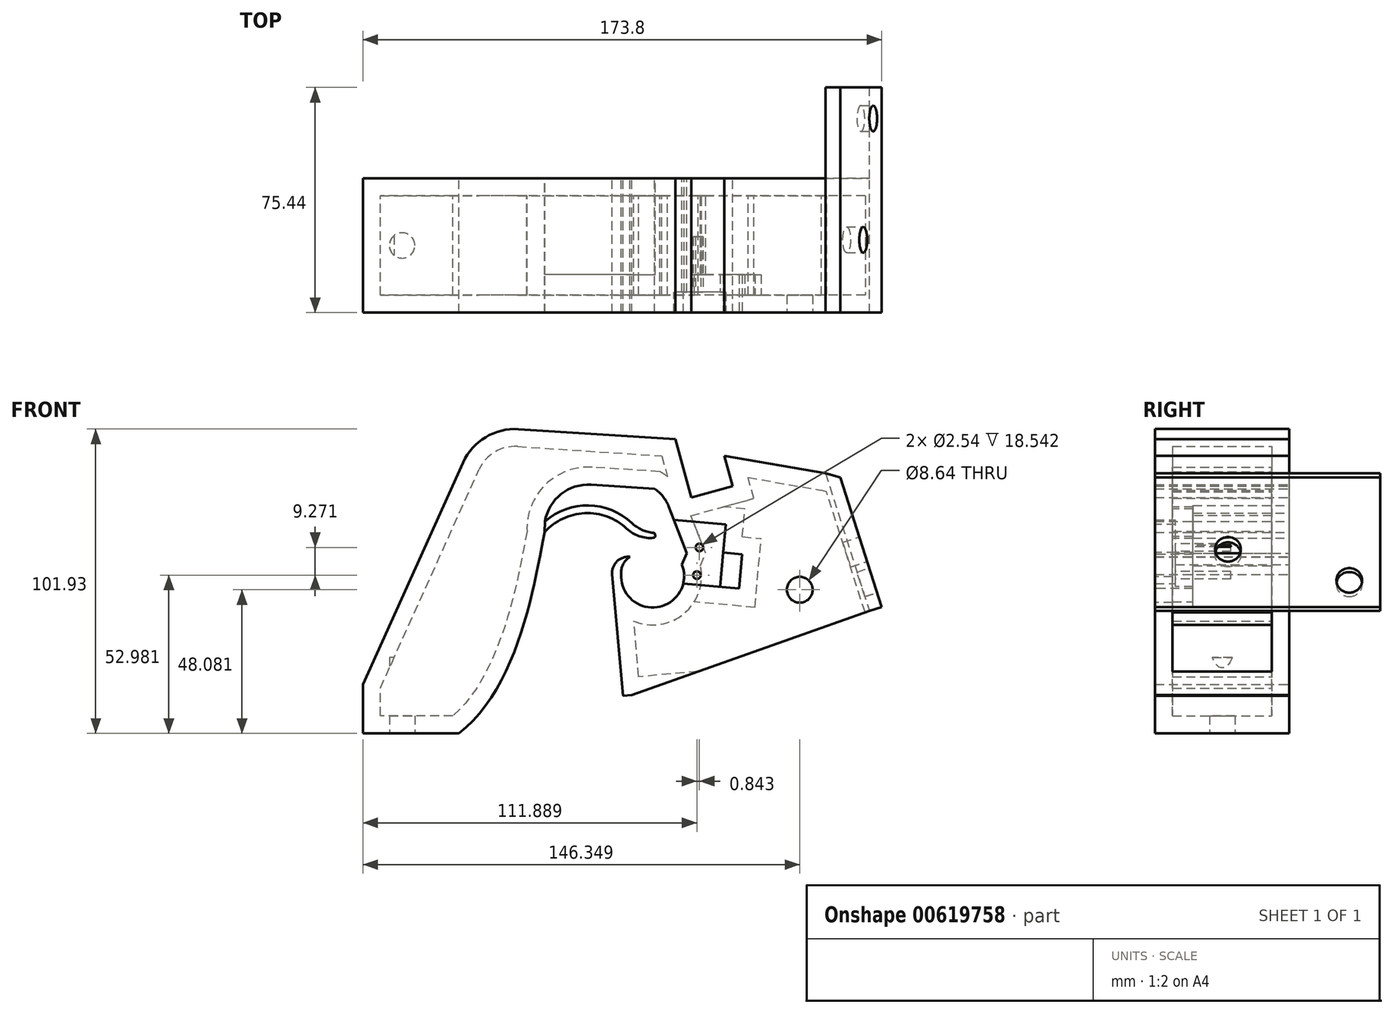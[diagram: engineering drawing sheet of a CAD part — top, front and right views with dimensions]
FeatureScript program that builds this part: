
annotation { "Feature Type Name" : "Feature", "Feature Type Description" : "" }
export const myFeature = defineFeature(function(context is Context, id is Id, definition is map)
    precondition{}
    {
        {
            var Q0;
            Q0=qCreatedBy(makeId("Front.planeOp"),FACE);
            var sketch = newSketch(context, id + "F0", { "sketchPlane" : qUnion([Q0])});
            skLineSegment(sketch, "E0", {"start": v(-44.32, -75.48) * mm, "end": v(-76.5, -75.48) * mm});
            skLineSegment(sketch, "E1", {"start": v(-76.5, -75.48) * mm, "end": v(-76.5, -59.1) * mm});
            skLineSegment(sketch, "E2", {"start": v(-76.5, -59.1) * mm, "end": v(-42.93, 15.25) * mm});
            skLineSegment(sketch, "E3", {"start": v(-24.33, 26.41) * mm, "end": v(28.17, 23.01) * mm});
            skLineSegment(sketch, "E4", {"start": v(28.17, 23.01) * mm, "end": v(33.5, 3.51) * mm});
            skLineSegment(sketch, "E5", {"start": v(33.5, 3.51) * mm, "end": v(47.3, 7.28) * mm});
            skLineSegment(sketch, "E6", {"start": v(47.3, 7.28) * mm, "end": v(44.5, 17.52) * mm});
            skLineSegment(sketch, "E7", {"start": v(44.5, 17.52) * mm, "end": v(78.44, 11.64) * mm});
            skLineSegment(sketch, "E8", {"start": v(93.17, -34.52) * mm, "end": v(13.6, -62.6) * mm});
            skLineSegment(sketch, "E9", {"start": v(10.3, -25.22) * mm, "end": v(10.04, -22.24) * mm});
            skPoint(sketch, "E10", {"position": v(20.57, -22.81) * mm});
            skArc(sketch, "E11", {"start": v(10.04, -22.24) * mm, "mid": v(22.25, -33.23) * mm, "end": v(30.39, -18.96) * mm});
            skArc(sketch, "E12", {"start": v(10.04, -22.24) * mm, "mid": v(10.66, -18.9) * mm, "end": v(12.94, -16.38) * mm});
            skLineSegment(sketch, "E13", {"start": v(30.39, -18.96) * mm, "end": v(32.03, -15.11) * mm});
            skLineSegment(sketch, "E14", {"start": v(32.03, -15.11) * mm, "end": v(25.9, 0.62) * mm});
            skArc(sketch, "E15", {"start": v(25.9, 0.62) * mm, "mid": v(24, 3.89) * mm, "end": v(21.2, 6.44) * mm});
            skLineSegment(sketch, "E16", {"start": v(21.2, 6.44) * mm, "end": v(0, 7.81) * mm});
            skArc(sketch, "E17", {"start": v(0, 7.81) * mm, "mid": v(-10.11, 4.65) * mm, "end": v(-15.5, -4.47) * mm});
            skFitSpline(sketch, "E18", {"points": [v(-15.65, -8.2) * mm, v(-44.32, -75.48) * mm], "startDerivative": vector(-10.53, -56.17) * mm, "endDerivative": vector(-57.92, -43.88) * mm});
            skLineSegment(sketch, "E19", {"start": v(13.6, -62.6) * mm, "end": v(10.6, -62.87) * mm});
            skLineSegment(sketch, "E20", {"start": v(10.6, -62.87) * mm, "end": v(7, -22.24) * mm});
            skArc(sketch, "E21", {"start": v(7, -22.24) * mm, "mid": v(8.6, -17.92) * mm, "end": v(12.94, -16.38) * mm});
            skArc(sketch, "E22", {"start": v(11.85, -6.91) * mm, "mid": v(-2.17, -1.71) * mm, "end": v(-15.65, -8.2) * mm});
            skArc(sketch, "E23", {"start": v(11.85, -6.91) * mm, "mid": v(16.02, -9.43) * mm, "end": v(20.86, -10) * mm});
            skArc(sketch, "E24.0", {"start": v(13.6, -5.06) * mm, "mid": v(-0.84, 0.84) * mm, "end": v(-15.5, -4.47) * mm});
            skArc(sketch, "E25", {"start": v(13.6, -5.06) * mm, "mid": v(16.93, -7.3) * mm, "end": v(20.8, -8.32) * mm});
            skLineSegment(sketch, "E26", {"start": v(93.17, -34.52) * mm, "end": v(97.3, -33.2) * mm});
            skLineSegment(sketch, "E27", {"start": v(97.3, -33.2) * mm, "end": v(83.43, 10.23) * mm});
            skLineSegment(sketch, "E28", {"start": v(83.43, 10.23) * mm, "end": v(78.44, 11.64) * mm});
            skPoint(sketch, "E29.visualSharp", {"position": v(-37.5, 27.27) * mm});
            skArc(sketch, "E29.filletArc", {"start": v(-24.33, 26.41) * mm, "mid": v(-35.38, 23.73) * mm, "end": v(-42.93, 15.25) * mm});
            skLineSegment(sketch, "E30", {"start": v(78.44, 11.64) * mm, "end": v(93.17, -34.52) * mm});
            skLineSegment(sketch, "E31", {"start": v(21.38, -8.87) * mm, "end": v(21.43, -9.3) * mm});
            skPoint(sketch, "E32.orphan", {"position": v(27.65, -6.91) * mm});
            skPoint(sketch, "E33.visualSharp", {"position": v(21.32, -8.35) * mm});
            skArc(sketch, "E33.filletArc", {"start": v(21.38, -8.87) * mm, "mid": v(21.2, -8.5) * mm, "end": v(20.8, -8.32) * mm});
            skPoint(sketch, "E34.visualSharp", {"position": v(21.5, -9.92) * mm});
            skArc(sketch, "E34.filletArc", {"start": v(20.86, -10) * mm, "mid": v(21.3, -9.76) * mm, "end": v(21.43, -9.3) * mm});
            skSolve(sketch);
        }
        {
            var Q0;
            Q0=makeQuery(id+"F0.imprint","IMPRINT",FACE,{"disambiguationData":[TD([[makeQuery(id+"F0.imprint","IMPRINT",EDGE,{"derivedFrom":sQuery(id+"F0.wireOp",EDGE,"E0")}),-1.0]])]});
            extrude(context, id + "F1", {"entities" : qUnion([Q0]), "endBound" : BoundingType.SYMMETRIC, "depth" : 44.96 * mm, "offsetDistance" : 25.4 * mm});
        }
        {
            var Q0;
            Q0=makeQuery(id+"F0.imprint","IMPRINT",FACE,{"disambiguationData":[TD([[makeQuery(id+"F0.imprint","IMPRINT",EDGE,{"derivedFrom":sQuery(id+"F0.wireOp",EDGE,"E26")}),1.0]])]});
            extrude(context, id + "F2", {"entities" : qUnion([Q0]), "operationType" : NewBodyOperationType.ADD, "depth" : 22.48 * mm, "offsetDistance" : 25.4 * mm, "hasSecondDirection" : true, "secondDirectionOppositeDirection" : true, "secondDirectionDepth" : 52.96 * mm});
        }
        {
            var Q0;
            {var subQ0=sQuery(id+"F0.wireOp",EDGE,"E30");Q0=makeQuery(id+"F2.boolean.opBoolean","MERGE",FACE,{"derivedFrom":[makeQuery(id+"F1.opExtrude","CAP_FACE",FACE,{"disambiguationData":[OSD([sQuery(id+"F0.wireOp",EDGE,"E0"),sQuery(id+"F0.wireOp",EDGE,"E1"),sQuery(id+"F0.wireOp",EDGE,"E2"),sQuery(id+"F0.wireOp",EDGE,"E3"),sQuery(id+"F0.wireOp",EDGE,"E4"),sQuery(id+"F0.wireOp",EDGE,"E5"),sQuery(id+"F0.wireOp",EDGE,"E6"),sQuery(id+"F0.wireOp",EDGE,"E7"),sQuery(id+"F0.wireOp",EDGE,"E8"),sQuery(id+"F0.wireOp",EDGE,"E11"),sQuery(id+"F0.wireOp",EDGE,"E12"),sQuery(id+"F0.wireOp",EDGE,"E13"),sQuery(id+"F0.wireOp",EDGE,"E14"),sQuery(id+"F0.wireOp",EDGE,"E15"),sQuery(id+"F0.wireOp",EDGE,"E16"),sQuery(id+"F0.wireOp",EDGE,"E17"),sQuery(id+"F0.wireOp",EDGE,"E18"),sQuery(id+"F0.wireOp",EDGE,"E19"),sQuery(id+"F0.wireOp",EDGE,"E20"),sQuery(id+"F0.wireOp",EDGE,"E21"),sQuery(id+"F0.wireOp",EDGE,"E22"),sQuery(id+"F0.wireOp",EDGE,"E23"),sQuery(id+"F0.wireOp",EDGE,"E24.0"),sQuery(id+"F0.wireOp",EDGE,"E25"),sQuery(id+"F0.wireOp",EDGE,"E29.filletArc"),subQ0])],"isStart":false}),makeQuery(id+"F2.opExtrude","CAP_FACE",FACE,{"disambiguationData":[OSD([sQuery(id+"F0.wireOp",EDGE,"E26"),sQuery(id+"F0.wireOp",EDGE,"E27"),sQuery(id+"F0.wireOp",EDGE,"E28"),subQ0])],"isStart":false})]});}
            var sketch = newSketch(context, id + "F3", { "sketchPlane" : qUnion([Q0])});
            skLineSegment(sketch, "E35", {"start": v(-15.5, -4.47) * mm, "end": v(-15.65, -8.2) * mm});
            skSolve(sketch);
        }
        {
            var Q0;
            Q0=makeQuery(id+"F1.opExtrude","CAP_FACE",FACE,{"disambiguationData":[OSD([sQuery(id+"F0.wireOp",EDGE,"E0"),sQuery(id+"F0.wireOp",EDGE,"E1"),sQuery(id+"F0.wireOp",EDGE,"E2"),sQuery(id+"F0.wireOp",EDGE,"E3"),sQuery(id+"F0.wireOp",EDGE,"E4"),sQuery(id+"F0.wireOp",EDGE,"E5"),sQuery(id+"F0.wireOp",EDGE,"E6"),sQuery(id+"F0.wireOp",EDGE,"E7"),sQuery(id+"F0.wireOp",EDGE,"E8"),sQuery(id+"F0.wireOp",EDGE,"E11"),sQuery(id+"F0.wireOp",EDGE,"E12"),sQuery(id+"F0.wireOp",EDGE,"E13"),sQuery(id+"F0.wireOp",EDGE,"E14"),sQuery(id+"F0.wireOp",EDGE,"E15"),sQuery(id+"F0.wireOp",EDGE,"E16"),sQuery(id+"F0.wireOp",EDGE,"E17"),sQuery(id+"F0.wireOp",EDGE,"E18"),sQuery(id+"F0.wireOp",EDGE,"E19"),sQuery(id+"F0.wireOp",EDGE,"E20"),sQuery(id+"F0.wireOp",EDGE,"E21"),sQuery(id+"F0.wireOp",EDGE,"E22"),sQuery(id+"F0.wireOp",EDGE,"E23"),sQuery(id+"F0.wireOp",EDGE,"E24.0"),sQuery(id+"F0.wireOp",EDGE,"E25"),sQuery(id+"F0.wireOp",EDGE,"E29.filletArc"),sQuery(id+"F0.wireOp",EDGE,"E30")])],"isStart":true});
            var sketch = newSketch(context, id + "F4", { "sketchPlane" : qUnion([Q0])});
            skLineSegment(sketch, "E36", {"start": v(15.5, -4.47) * mm, "end": v(15.65, -8.2) * mm});
            skLineSegment(sketch, "E37", {"start": v(-27.89, -23.7) * mm, "end": v(-43.3, -25.26) * mm});
            skLineSegment(sketch, "E38", {"start": v(-43.3, -25.26) * mm, "end": v(-45.8, -0.52) * mm});
            skLineSegment(sketch, "E39", {"start": v(-45.8, -0.52) * mm, "end": v(-30.39, 1.04) * mm});
            skCircle(sketch, "E40", {"center": v(-36.45, -12.14) * mm, "radius": 1.27 * mm});
            skCircle(sketch, "E41", {"center": v(-35.52, -21.4) * mm, "radius": 1.27 * mm});
            skLineSegment(sketch, "E42.0", {"start": v(-24.07, 1.68) * mm, "end": v(-21.57, -23.06) * mm});
            skLineSegment(sketch, "E43", {"start": v(-24.07, 1.68) * mm, "end": v(-30.39, 1.04) * mm});
            skLineSegment(sketch, "E44", {"start": v(-21.57, -23.06) * mm, "end": v(-27.89, -23.7) * mm});
            skLineSegment(sketch, "E45.0", {"start": v(-49.62, -25.9) * mm, "end": v(-50.64, -15.8) * mm});
            skLineSegment(sketch, "E46", {"start": v(-43.3, -25.26) * mm, "end": v(-49.62, -25.9) * mm});
            skLineSegment(sketch, "E47", {"start": v(-44.32, -15.16) * mm, "end": v(-50.64, -15.8) * mm});
            skSolve(sketch);
        }
        {
            var Q0;
            Q0=makeQuery(id+"F3.imprint","IMPRINT",FACE,{"disambiguationData":[TD([[makeQuery(id+"F3.imprint","IMPRINT",EDGE,{"derivedFrom":sQuery(id+"F3.wireOp",EDGE,"E35")}),-1.0]])]});
            var sketch = newSketch(context, id + "F5", { "sketchPlane" : qUnion([Q0])});
            skLineSegment(sketch, "E48", {"start": v(22.8, -24.54) * mm, "end": v(43.2, -26.4) * mm});
            skLineSegment(sketch, "E49", {"start": v(43.2, -26.4) * mm, "end": v(45.1, -5.56) * mm});
            skLineSegment(sketch, "E50", {"start": v(45.1, -5.56) * mm, "end": v(23.51, -3.6) * mm});
            skLineSegment(sketch, "E51", {"start": v(23.51, -3.6) * mm, "end": v(21.61, -24.54) * mm});
            skLineSegment(sketch, "E52", {"start": v(21.61, -24.54) * mm, "end": v(22.8, -24.54) * mm});
            skCircle(sketch, "E53", {"center": v(35.39, -22.5) * mm, "radius": 1.27 * mm});
            skCircle(sketch, "E54", {"center": v(36.23, -13.23) * mm, "radius": 1.27 * mm});
            skLineSegment(sketch, "E55.0", {"start": v(49.52, -26.97) * mm, "end": v(50.56, -15.5) * mm});
            skLineSegment(sketch, "E56", {"start": v(44.24, -14.92) * mm, "end": v(50.56, -15.5) * mm});
            skLineSegment(sketch, "E57", {"start": v(49.52, -26.97) * mm, "end": v(43.2, -26.4) * mm});
            skSolve(sketch);
        }
        {
            var Q0;
            Q0 = qSketchRegion(id + "F5", true);
            extrude(context, id + "F6", {"entities" : qUnion([Q0]), "operationType" : NewBodyOperationType.REMOVE, "oppositeDirection" : true, "depth" : 6.86 * mm, "offsetDistance" : 25.4 * mm});
        }
        {
            var Q0;
            Q0=makeQuery(id+"F1.opExtrude","SWEPT_FACE",FACE,{"disambiguationData":[OSD([sQuery(id+"F0.wireOp",EDGE,"E8")])]});
            shell(context, id + "F7", {"entities" : qUnion([Q0]), "thickness" : 5.84 * mm});
        }
        {
            var Q0;
            Q0=makeQuery(id+"F5.imprint","IMPRINT",FACE,{"disambiguationData":[TD([[makeQuery(id+"F5.imprint","IMPRINT",EDGE,{"derivedFrom":sQuery(id+"F5.wireOp",EDGE,"E55.0")}),1.0]])]});
            extrude(context, id + "F8", {"entities" : qUnion([Q0]), "operationType" : NewBodyOperationType.REMOVE, "oppositeDirection" : true, "depth" : 12.7 * mm, "offsetDistance" : 25.4 * mm});
        }
        {
            var Q0;
            Q0=makeQuery(id+"F5.imprint","IMPRINT",FACE,{"disambiguationData":[TD([[makeQuery(id+"F5.imprint","IMPRINT",EDGE,{"derivedFrom":sQuery(id+"F5.wireOp",EDGE,"E53")}),1.0]])]});
            var Q1;
            Q1=makeQuery(id+"F5.imprint","IMPRINT",FACE,{"disambiguationData":[TD([[makeQuery(id+"F5.imprint","IMPRINT",EDGE,{"derivedFrom":sQuery(id+"F5.wireOp",EDGE,"E54")}),1.0]])]});
            extrude(context, id + "F9", {"entities" : qUnion([Q0, Q1]), "operationType" : NewBodyOperationType.REMOVE, "oppositeDirection" : true, "depth" : 25.4 * mm, "offsetDistance" : 25.4 * mm});
        }
        {
            var Q0;
            Q0=makeQuery(id+"F3.imprint","IMPRINT",FACE,{"disambiguationData":[TD([[makeQuery(id+"F3.imprint","IMPRINT",EDGE,{"derivedFrom":sQuery(id+"F3.wireOp",EDGE,"E35")}),1.0]])]});
            extrude(context, id + "F10", {"entities" : qUnion([Q0]), "operationType" : NewBodyOperationType.REMOVE, "endBound" : BoundingType.SYMMETRIC, "oppositeDirection" : true, "depth" : 25.4 * mm, "offsetDistance" : 25.4 * mm});
        }
        {
            var Q0;
            Q0=makeQuery(id+"F4.imprint","IMPRINT",FACE,{"disambiguationData":[TD([[makeQuery(id+"F4.imprint","IMPRINT",EDGE,{"derivedFrom":sQuery(id+"F4.wireOp",EDGE,"E36")}),-1.0]])]});
            extrude(context, id + "F11", {"entities" : qUnion([Q0]), "operationType" : NewBodyOperationType.REMOVE, "oppositeDirection" : true, "depth" : 1 / 50.8 * mm, "offsetDistance" : 25.4 * mm});
        }
        {
            var Q0;
            Q0=makeQuery(id+"F1.opExtrude","SWEPT_FACE",FACE,{"disambiguationData":[OSD([sQuery(id+"F0.wireOp",EDGE,"E0")])]});
            var sketch = newSketch(context, id + "F12", { "sketchPlane" : qUnion([Q0])});
            skCircle(sketch, "E58", {"center": v(-63.36, 0) * mm, "radius": 4.25 * mm});
            skSolve(sketch);
        }
        {
            var Q0;
            Q0=makeQuery(id+"F12.imprint","IMPRINT",FACE,{"disambiguationData":[TD([[makeQuery(id+"F12.imprint","IMPRINT",EDGE,{"derivedFrom":sQuery(id+"F12.wireOp",EDGE,"E58")}),1.0]])]});
            extrude(context, id + "F13", {"entities" : qUnion([Q0]), "operationType" : NewBodyOperationType.REMOVE, "oppositeDirection" : true, "depth" : 25.4 * mm, "offsetDistance" : 25.4 * mm});
        }
        {
            var Q0;
            Q0=makeQuery(id+"F2.opExtrude","SWEPT_FACE",FACE,{"disambiguationData":[OSD([sQuery(id+"F0.wireOp",EDGE,"E27")])]});
            var sketch = newSketch(context, id + "F14", { "sketchPlane" : qUnion([Q0])});
            skCircle(sketch, "E59", {"center": v(1.9, -40.9) * mm, "radius": 4.32 * mm});
            skCircle(sketch, "E60", {"center": v(42.55, -51.83) * mm, "radius": 4.32 * mm});
            skSolve(sketch);
        }
        {
            var Q0;
            Q0=makeQuery(id+"F14.imprint","IMPRINT",FACE,{"disambiguationData":[TD([[makeQuery(id+"F14.imprint","IMPRINT",EDGE,{"derivedFrom":sQuery(id+"F14.wireOp",EDGE,"E59")}),1.0]])]});
            var Q1;
            Q1=makeQuery(id+"F14.imprint","IMPRINT",FACE,{"disambiguationData":[TD([[makeQuery(id+"F14.imprint","IMPRINT",EDGE,{"derivedFrom":sQuery(id+"F14.wireOp",EDGE,"E60")}),1.0]])]});
            extrude(context, id + "F15", {"entities" : qUnion([Q0, Q1]), "operationType" : NewBodyOperationType.REMOVE, "oppositeDirection" : true, "depth" : 10.16 * mm, "offsetDistance" : 25.4 * mm});
        }
        {
            var Q0;
            {var subQ0=sQuery(id+"F0.wireOp",EDGE,"E24.0");var subQ1=sQuery(id+"F0.wireOp",EDGE,"E22");var subQ2=sQuery(id+"F0.wireOp",EDGE,"E21");var subQ3=sQuery(id+"F0.wireOp",EDGE,"E20");var subQ4=sQuery(id+"F0.wireOp",EDGE,"E19");var subQ5=sQuery(id+"F0.wireOp",EDGE,"E18");var subQ6=sQuery(id+"F0.wireOp",EDGE,"E17");var subQ7=sQuery(id+"F0.wireOp",EDGE,"E16");var subQ8=sQuery(id+"F0.wireOp",EDGE,"E15");var subQ9=sQuery(id+"F0.wireOp",EDGE,"E14");var subQ10=sQuery(id+"F0.wireOp",EDGE,"E12");var subQ11=sQuery(id+"F0.wireOp",EDGE,"E2");var subQ12=sQuery(id+"F0.wireOp",EDGE,"E1");var subQ13=sQuery(id+"F0.wireOp",EDGE,"E3");var subQ14=sQuery(id+"F0.wireOp",EDGE,"E23");var subQ15=sQuery(id+"F0.wireOp",EDGE,"E0");var subQ16=sQuery(id+"F0.wireOp",EDGE,"E11");var subQ17=sQuery(id+"F0.wireOp",EDGE,"E4");var subQ18=sQuery(id+"F0.wireOp",EDGE,"E5");var subQ19=sQuery(id+"F0.wireOp",EDGE,"E6");var subQ20=sQuery(id+"F0.wireOp",EDGE,"E7");var subQ21=sQuery(id+"F0.wireOp",EDGE,"E8");var subQ22=sQuery(id+"F0.wireOp",EDGE,"E25");var subQ23=sQuery(id+"F0.wireOp",EDGE,"E26");var subQ24=sQuery(id+"F0.wireOp",EDGE,"E29.filletArc");var subQ25=sQuery(id+"F0.wireOp",EDGE,"E31");var subQ26=sQuery(id+"F0.wireOp",EDGE,"E27");var subQ27=sQuery(id+"F0.wireOp",EDGE,"E33.filletArc");var subQ28=sQuery(id+"F0.wireOp",EDGE,"E28");var subQ29=sQuery(id+"F0.wireOp",EDGE,"E34.filletArc");var subQ30=sQuery(id+"F0.wireOp",EDGE,"E30");Q0=makeQuery(id+"F6.boolean.opBoolean","SPLIT",FACE,{"disambiguationData":[TD([makeQuery(id+"F1.opExtrude","SWEPT_FACE",FACE,{"disambiguationData":[OSD([subQ15])]})])],"derivedFrom":makeQuery(id+"F2.boolean.opBoolean","MERGE",FACE,{"derivedFrom":[makeQuery(id+"F1.opExtrude","CAP_FACE",FACE,{"disambiguationData":[OSD([subQ15,subQ12,subQ11,subQ13,subQ17,subQ18,subQ19,subQ20,subQ21,subQ16,subQ10,sQuery(id+"F0.wireOp",EDGE,"E13"),subQ9,subQ8,subQ7,subQ6,subQ5,subQ4,subQ3,subQ2,subQ1,subQ14,subQ0,subQ22,subQ24,subQ30,subQ25,subQ27,subQ29])],"isStart":false}),makeQuery(id+"F2.opExtrude","CAP_FACE",FACE,{"disambiguationData":[OSD([subQ23,subQ26,subQ28,subQ30])],"isStart":false})]})});}
            var sketch = newSketch(context, id + "F16", { "sketchPlane" : qUnion([Q0])});
            skCircle(sketch, "E61", {"center": v(69.85, -27.4) * mm, "radius": 4.32 * mm});
            skSolve(sketch);
        }
        {
            var Q0;
            Q0=makeQuery(id+"F16.imprint","IMPRINT",FACE,{"disambiguationData":[TD([[makeQuery(id+"F16.imprint","IMPRINT",EDGE,{"derivedFrom":sQuery(id+"F16.wireOp",EDGE,"E61")}),1.0]])]});
            extrude(context, id + "F17", {"entities" : qUnion([Q0]), "operationType" : NewBodyOperationType.REMOVE, "oppositeDirection" : true, "depth" : 7.62 * mm, "offsetDistance" : 25.4 * mm});
        }
    });
